# Revit family: Neptun Medius Parallel
name_source: partatom
category: HLS-Bauteile
units: mm (PartAtom-declared; Revit-internal decimal feet)

## family parameters
Arbeitsebenenbasiert = Nein
Beim Laden mit Abzugskörper schneiden = Nein
Bemaßung runder Anschluss = Durchmesser verwenden
Beschriftungsausrichtung beibehalten = Nein
Gemeinsam genutzt = Nein
Immer vertikal = Ja
Klassifizierung = Keine
Raumberechnungspunkt = Nein
Teiletyp = Normal

## types (7) — shared parameters
Anschluss 1" = 25 mm  [stored 0.082021 ft]
Datenblatt = https://www.burkhalter-h2o.ch
Homepage = https://www.burkhalter-h2o.ch
LUT = LUT_Neptun_Medius
Sockel_Höhe = 100 mm  [stored 0.328084 ft]
Steuerung_Breite = 175 mm  [stored 0.574147 ft]
Steuerung_Höhe = 225 mm  [stored 0.738189 ft]
Steuerung_Tiefe = 75 mm  [stored 0.246063 ft]
zero-valued in all types: Vorgabe-Ansicht

## per-type parameters (varying)
| type | A | B | Behälterkopf | C | Harzinhalt_pro_Harzdruckbehälter | Sockel_Absatz_Oben | Sockel_Absatz_Unten | X |
| Neptun Medius - 25L | 257 mm  [stored 0.843176 ft] | 1100 mm  [stored 3.60892 ft] | 100 mm  [stored 0.328084 ft] | 960 mm  [stored 3.14961 ft] | 25L | 139 mm | 139 mm | 400 mm  [stored 1.31234 ft] |
| Neptun Medius - 50L | 304 mm  [stored 0.997375 ft] | 1430 mm  [stored 4.6916 ft] | 150 mm  [stored 0.492126 ft] | 1290 mm  [stored 4.23228 ft] | 50L | 162 mm  [stored 0.531496 ft] | 162 mm  [stored 0.531496 ft] | 400 mm  [stored 1.31234 ft] |
| Neptun Medius - 75L | 369 mm  [stored 1.21063 ft] | 1880 mm  [stored 6.16798 ft] | 150 mm  [stored 0.492126 ft] | 1740 mm  [stored 5.70866 ft] | 75L | 195 mm  [stored 0.639764 ft] | 195 mm  [stored 0.639764 ft] | 450 mm  [stored 1.47638 ft] |
| Neptun Medius - 100L | 406 mm  [stored 1.33202 ft] | 1880 mm  [stored 6.16798 ft] | 200 mm  [stored 0.656168 ft] | 1740 mm  [stored 5.70866 ft] | 100L | 213 mm  [stored 0.698819 ft] | 213 mm  [stored 0.698819 ft] | 500 mm  [stored 1.64042 ft] |
| Neptun Medius - 125L | 406 mm  [stored 1.33202 ft] | 1880 mm  [stored 6.16798 ft] | 200 mm  [stored 0.656168 ft] | 1740 mm  [stored 5.70866 ft] | 125L | 213 mm  [stored 0.698819 ft] | 213 mm  [stored 0.698819 ft] | 500 mm  [stored 1.64042 ft] |
| Neptun Medius - 150L | 552 mm  [stored 1.81102 ft] | 1840 mm  [stored 6.03675 ft] | 250 mm  [stored 0.82021 ft] | 1700 mm  [stored 5.57743 ft] | 150L | 286 mm | 286 mm | 650 mm  [stored 2.13255 ft] |
| Neptun Medius - 200L | 552 mm  [stored 1.81102 ft] | 1840 mm  [stored 6.03675 ft] | 250 mm  [stored 0.82021 ft] | 1700 mm  [stored 5.57743 ft] | 200L | 286 mm | 286 mm | 650 mm  [stored 2.13255 ft] |

note: [stored X ft] marks values corroborated as IEEE doubles in the binary element streams (Revit-internal decimal feet)
